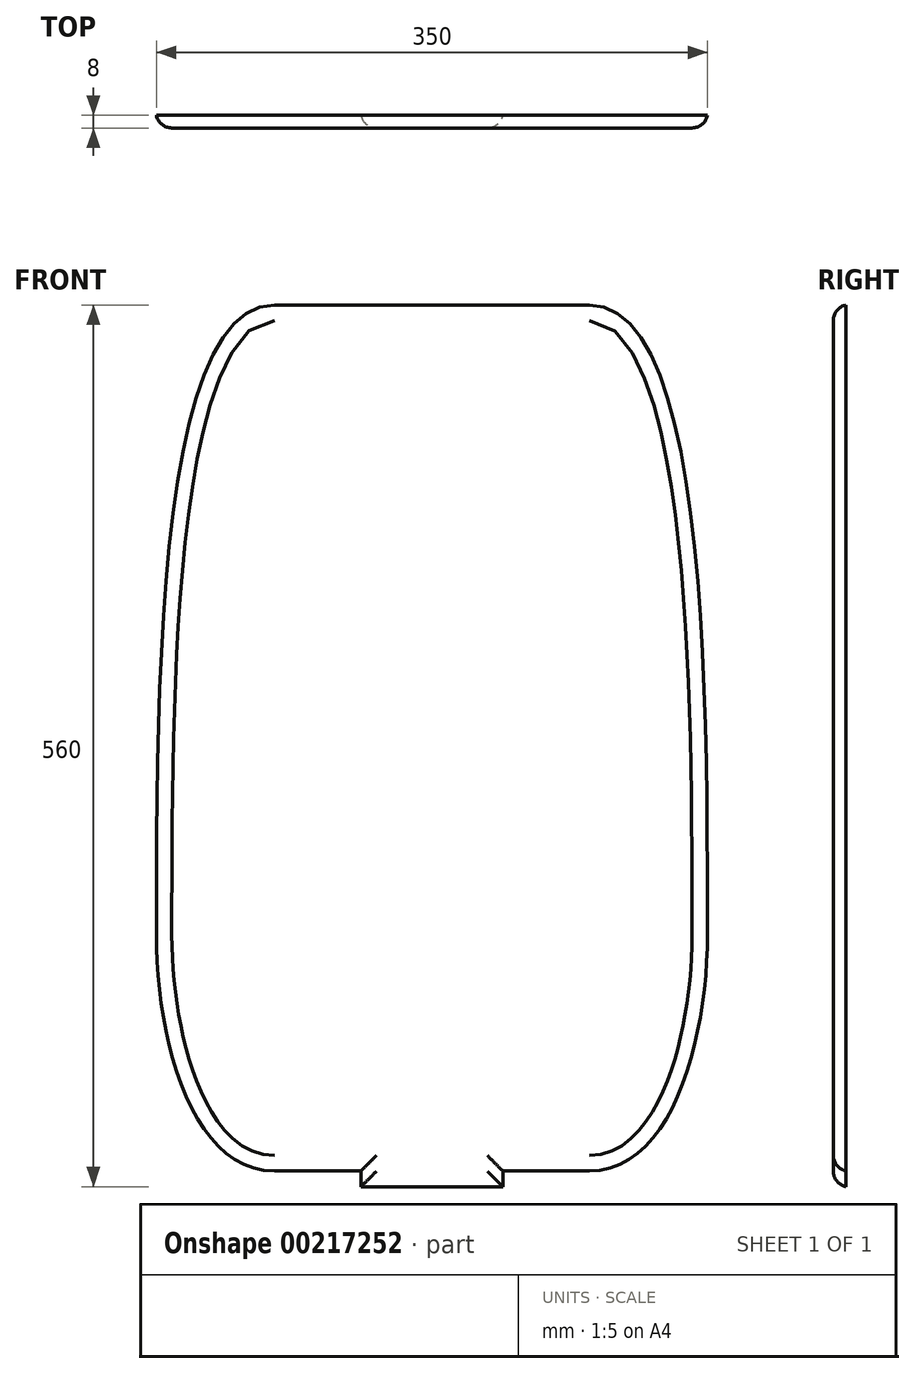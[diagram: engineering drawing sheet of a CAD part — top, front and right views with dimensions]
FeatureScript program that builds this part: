
annotation { "Feature Type Name" : "Feature", "Feature Type Description" : "" }
export const myFeature = defineFeature(function(context is Context, id is Id, definition is map)
    precondition{}
    {
        {
            var Q0;
            Q0=qCreatedBy(makeId("Front.planeOp"),FACE);
            var sketch = newSketch(context, id + "F0", { "sketchPlane" : qUnion([Q0])});
            skPoint(sketch, "E0.middle", {"position": v(10, -2.47) * mm});
            skFitSpline(sketch, "E1", {"points": [v(-90, 272.53) * mm, v(-165, -127.47) * mm], "startDerivative": vector(-225, 0) * mm, "endDerivative": vector(0, -458.8) * mm});
            skFitSpline(sketch, "E2", {"points": [v(-90, -277.47) * mm, v(-165, -127.47) * mm], "startDerivative": vector(-161.54, 0) * mm, "endDerivative": vector(0, 190.04) * mm});
            skFitSpline(sketch, "E3.MirrorCS", {"points": [v(110, 272.53) * mm, v(185, -127.47) * mm], "startDerivative": vector(225, 0) * mm, "endDerivative": vector(0, -458.8) * mm});
            skFitSpline(sketch, "E4.MirrorCS", {"points": [v(110, -277.47) * mm, v(185, -127.47) * mm], "startDerivative": vector(161.54, 0) * mm, "endDerivative": vector(0, 190.04) * mm});
            skLineSegment(sketch, "E5", {"start": v(-90, 272.53) * mm, "end": v(110, 272.53) * mm});
            skLineSegment(sketch, "E6", {"start": v(-90, -277.47) * mm, "end": v(110, -277.47) * mm});
            skLineSegment(sketch, "E7", {"start": v(-35, -287.47) * mm, "end": v(-35, -277.47) * mm});
            skLineSegment(sketch, "E8", {"start": v(55, -287.47) * mm, "end": v(55, -277.47) * mm});
            skLineSegment(sketch, "E9", {"start": v(-35, -287.47) * mm, "end": v(55, -287.47) * mm});
            skSolve(sketch);
        }
        {
            var Q0;
            Q0 = qSketchRegion(id + "F0", true);
            extrude(context, id + "F1", {"entities" : qUnion([Q0]), "depth" : 8 * mm});
        }
        {
            var Q0;
            Q0=makeQuery(id+"F1.opExtrude","CAP_FACE",FACE,{"disambiguationData":[OSD([sQuery(id+"F0.wireOp",EDGE,"E1"),sQuery(id+"F0.wireOp",EDGE,"E2"),sQuery(id+"F0.wireOp",EDGE,"E3.MirrorCS"),sQuery(id+"F0.wireOp",EDGE,"E4.MirrorCS"),sQuery(id+"F0.wireOp",EDGE,"E5"),sQuery(id+"F0.wireOp",EDGE,"E6"),sQuery(id+"F0.wireOp",EDGE,"E7"),sQuery(id+"F0.wireOp",EDGE,"E8"),sQuery(id+"F0.wireOp",EDGE,"E9")])],"isStart":false});
            fillet(context, id + "F2", {"entities" : qUnion([Q0]), "radius" : 10 * mm, "tangentPropagation" : true, "allowEdgeOverflow" : false});
        }
    });
